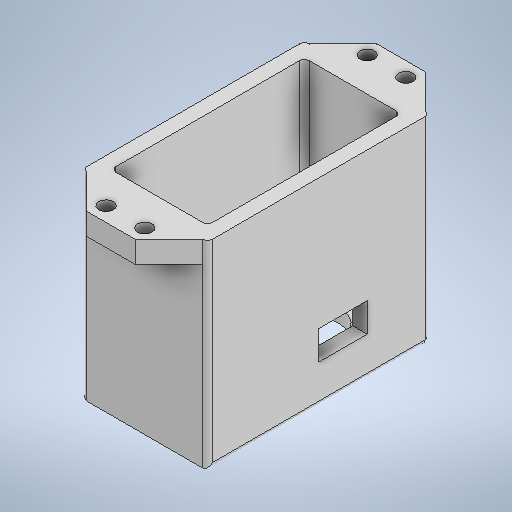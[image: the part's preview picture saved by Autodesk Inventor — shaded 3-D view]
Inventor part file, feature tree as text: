
AUTODESK INVENTOR PART (.ipt)
format: ipt  version: 2025.2 (Build 292293000, 293)  size: 309,248 bytes
history: native  units: in
note: dims shown in document units (in); Inventor stores cm internally (conversion verified against a paired STEP export)
features: other x3, extrude x2, sketch x2, chamfer x1
ambient origin geometry x8: Origin, YZ Plane, XZ Plane, XY Plane, X Axis, Y Axis, Z Axis, Center Point
bodies: Solid1 (feature_tree)
feature tree (8):
  other  "servo_holder.ipt"
  extrude  "Extrusion1"  Depth=0.3937in
  extrude  "Extrusion2"  Depth=0.2756in
  chamfer  "Chamfer1"  Distance=0.2756in
  other  "Solid1::servo_holder.ipt"
  other  "TaggingFeature1"
  sketch  "Sketch1"  dims[d0=0.3937in d1=0.9449in]
  sketch  "Sketch2"  dims[d2=0.2756in d3=0.9449in d4=0.2756in d5=0.1772in d6=0.0in d7=0.315in d8=2.126in d9=0.2362in d10=0.2756in d11=0.1181in d12=0.1181in d13=0.1181in d14=0.1181in d15=0.0in d16=0.0in d17=0.2756in d18=0.0787in d19=45.0deg]
